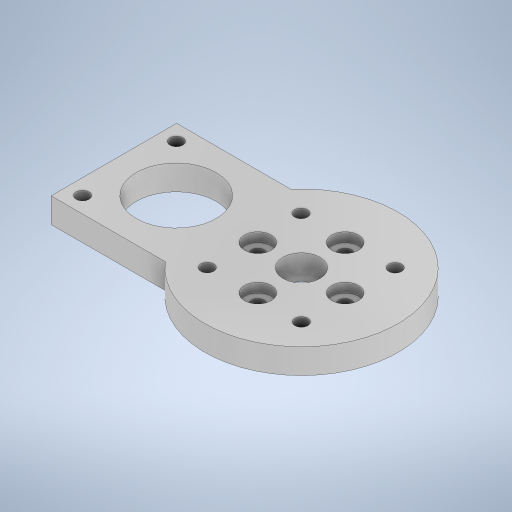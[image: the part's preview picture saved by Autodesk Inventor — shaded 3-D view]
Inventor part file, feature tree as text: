
AUTODESK INVENTOR PART (.ipt)
format: ipt  version: 2024.2 (Build 282272000, 272)  size: 311,808 bytes
history: native  units: in
note: dims shown in document units (in); Inventor stores cm internally (conversion verified against a paired STEP export)
features: sketch x6, reference x6, extrude x4, other x4, hole x2
ambient origin geometry x8: Origin, YZ Plane, XZ Plane, XY Plane, X Axis, Y Axis, Z Axis, Center Point
bodies: Solid1 (feature_tree)
feature tree (22):
  extrude  "Extrusion1"  Depth=0.7929in
  extrude  "Extrusion2"  Depth=0.1575in
  extrude  "Extrusion4"  Depth=1.2205in
  hole  "Hole4"  [1 undecoded]
  extrude  "Extrusion5"  [1 undecoded]
  hole  "Hole5"  [1 undecoded]
  sketch  "Sketch1"  dims[d0=1.5787in d1=0.7929in]
  sketch  "Sketch3"  dims[d2=0.1575in d3=0.0in d11=0.5118in]
  reference  "Reference3"
  sketch  "Sketch7"  dims[d12=0.0in d13=0.0in d31=1.2205in]
  reference  "Reference9"
  sketch  "Sketch8"  dims[d32=0.3937in d33=0.0in]
  reference  "Reference10"
  sketch  "Sketch9"  dims[d34=0.0827in d35=0.2362in d36=0.1693in d37=0.0591in d38=90.0deg d39=0.315in d40=0.8108in d41=0.2343in]
  reference  "Reference11"
  reference  "Reference12"
  sketch  "Sketch10"  dims[d42=0.0in d43=0.0in d44=0.0827in d45=0.2362in d46=0.1693in d47=0.0591in d48=90.0deg d49=0.315in d50=0.8108in]
  reference  "Reference13"
  other  "gripper_test.iam"
  other  "HTD-45H:1"
  other  "테프론:1"
  other  "Top Horn:2"
note: 3 required parameter values undecoded (feature->parameter linkage not recoverable at this tier; creation-order binding heuristic only, values carry confidence <= 0.55)
